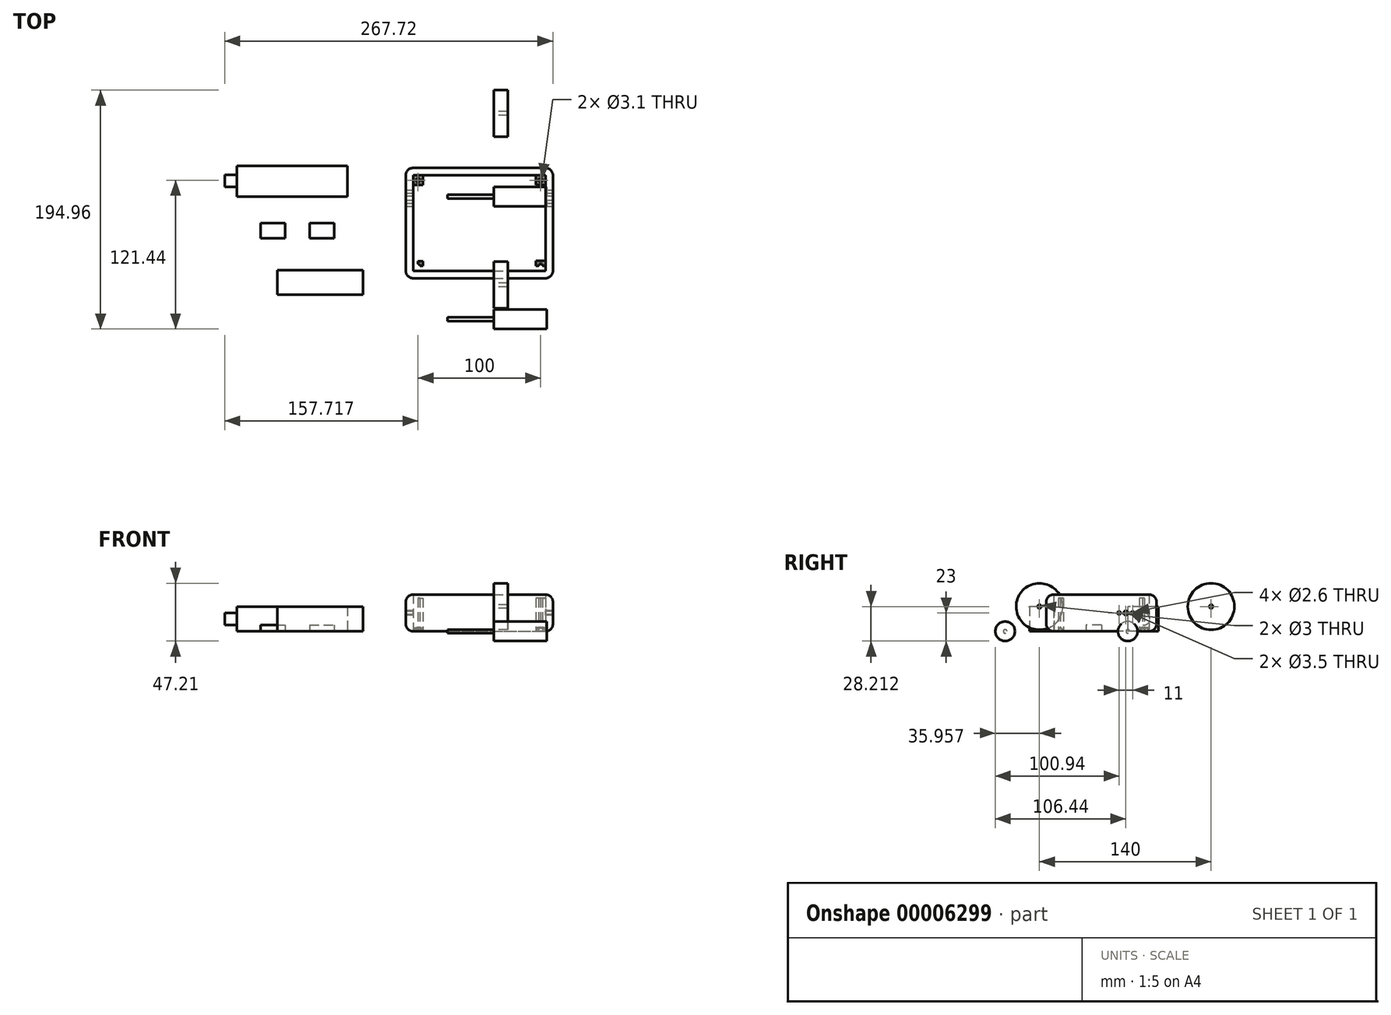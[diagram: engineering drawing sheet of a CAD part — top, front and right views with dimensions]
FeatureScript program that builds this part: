
annotation { "Feature Type Name" : "Feature", "Feature Type Description" : "" }
export const myFeature = defineFeature(function(context is Context, id is Id, definition is map)
    precondition{}
    {
        {
            var Q0;
            Q0=qCreatedBy(makeId("Top.planeOp"),FACE);
            var sketch = newSketch(context, id + "F0", { "sketchPlane" : qUnion([Q0])});
            skLineSegment(sketch, "E0.bottom", {"start": v(-71.87, 44.94) * mm, "end": v(48.13, 44.94) * mm});
            skLineSegment(sketch, "E0.top", {"start": v(-71.87, -45.06) * mm, "end": v(48.13, -45.06) * mm});
            skLineSegment(sketch, "E0.left", {"start": v(-71.87, 44.94) * mm, "end": v(-71.87, -45.06) * mm});
            skLineSegment(sketch, "E0.right", {"start": v(48.13, 44.94) * mm, "end": v(48.13, -45.06) * mm});
            skLineSegment(sketch, "E1.0", {"start": v(-65.87, 38.94) * mm, "end": v(42.13, 38.94) * mm});
            skLineSegment(sketch, "E1.1", {"start": v(-65.87, 38.94) * mm, "end": v(-65.87, -39.06) * mm});
            skLineSegment(sketch, "E1.2", {"start": v(-65.87, -39.06) * mm, "end": v(42.13, -39.06) * mm});
            skLineSegment(sketch, "E1.3", {"start": v(42.13, 38.94) * mm, "end": v(42.13, -39.06) * mm});
            skLineSegment(sketch, "E2.bottom", {"start": v(42.13, 38.94) * mm, "end": v(34.13, 38.94) * mm});
            skLineSegment(sketch, "E2.top", {"start": v(42.13, 30.94) * mm, "end": v(34.13, 30.94) * mm});
            skLineSegment(sketch, "E2.left", {"start": v(42.13, 38.94) * mm, "end": v(42.13, 30.94) * mm});
            skLineSegment(sketch, "E2.right", {"start": v(34.13, 38.94) * mm, "end": v(34.13, 30.94) * mm});
            skLineSegment(sketch, "E3.bottom", {"start": v(42.13, -39.06) * mm, "end": v(34.4, -39.06) * mm});
            skLineSegment(sketch, "E3.top", {"start": v(42.13, -31) * mm, "end": v(34.13, -31) * mm});
            skLineSegment(sketch, "E3.left", {"start": v(42.13, -39.06) * mm, "end": v(42.13, -31) * mm});
            skLineSegment(sketch, "E4.bottom", {"start": v(-65.87, 38.94) * mm, "end": v(-57.87, 38.94) * mm});
            skLineSegment(sketch, "E4.top", {"start": v(-65.87, 30.94) * mm, "end": v(-57.87, 30.94) * mm});
            skLineSegment(sketch, "E4.left", {"start": v(-65.87, 38.94) * mm, "end": v(-65.87, 30.94) * mm});
            skLineSegment(sketch, "E4.right", {"start": v(-57.87, 38.94) * mm, "end": v(-57.87, 30.94) * mm});
            skLineSegment(sketch, "E5.bottom", {"start": v(-65.87, -39.06) * mm, "end": v(-57.87, -39.06) * mm});
            skLineSegment(sketch, "E5.top", {"start": v(-65.87, -31.06) * mm, "end": v(-57.87, -31.06) * mm});
            skLineSegment(sketch, "E5.left", {"start": v(-65.87, -39.06) * mm, "end": v(-65.87, -31.06) * mm});
            skLineSegment(sketch, "E5.right", {"start": v(-57.87, -39.06) * mm, "end": v(-57.87, -31.06) * mm});
            skCircle(sketch, "E6", {"center": v(38.13, -35) * mm, "radius": 1.55 * mm});
            skLineSegment(sketch, "E7", {"start": v(38.13, -33.45) * mm, "end": v(38.13, -31) * mm});
            skCircle(sketch, "E8", {"center": v(38.13, 34.94) * mm, "radius": 1.55 * mm});
            skCircle(sketch, "E9", {"center": v(-61.87, 34.94) * mm, "radius": 1.55 * mm});
            skCircle(sketch, "E10", {"center": v(-61.87, -35.06) * mm, "radius": 1.55 * mm});
            skLineSegment(sketch, "E11", {"start": v(36.58, 34.94) * mm, "end": v(34.13, 34.94) * mm});
            skLineSegment(sketch, "E12", {"start": v(38.13, 33.4) * mm, "end": v(38.13, 30.94) * mm});
            skLineSegment(sketch, "E13", {"start": v(-60.32, 34.94) * mm, "end": v(-57.87, 34.94) * mm});
            skLineSegment(sketch, "E14", {"start": v(-61.87, 33.4) * mm, "end": v(-61.87, 30.94) * mm});
            skLineSegment(sketch, "E15", {"start": v(-61.87, -33.5) * mm, "end": v(-61.87, -31.06) * mm});
            skLineSegment(sketch, "E16", {"start": v(-60.32, -35.06) * mm, "end": v(-57.87, -35.06) * mm});
            skLineSegment(sketch, "E17", {"start": v(34.13, -31) * mm, "end": v(34.13, -39.06) * mm});
            skLineSegment(sketch, "E18", {"start": v(36.58, -35) * mm, "end": v(34.13, -35) * mm});
            skLineSegment(sketch, "E19", {"start": v(39.68, -35) * mm, "end": v(42.13, -35) * mm});
            skSolve(sketch);
        }
        {
            var Q0;
            Q0=makeQuery(id+"F0.imprint","IMPRINT",FACE,{"disambiguationData":[TD([[makeQuery(id+"F0.imprint","IMPRINT",EDGE,{"derivedFrom":sQuery(id+"F0.wireOp",EDGE,"E0.bottom")}),-1.0]])]});
            var Q1;
            {var subQ1=sQuery(id+"F0.wireOp",EDGE,"2364edff-3680-4c65-9d3e-53515021508b");Q1=makeQuery(id+"F0.imprint","IMPRINT",FACE,{"disambiguationData":[TD([[makeQuery(id+"F0.imprint","IMPRINT",EDGE,{"derivedFrom":subQ1}),-1.0]])]});}
            extrude(context, id + "F1", {"entities" : qUnion([Q0, Q1]), "depth" : 30 * mm});
        }
        {
            var Q0;
            {var subQ4=sQuery(id+"F0.wireOp",EDGE,"E4.bottom");Q0=makeQuery(id+"F0.imprint","IMPRINT",FACE,{"disambiguationData":[TD([[makeQuery(id+"F0.imprint","IMPRINT",EDGE,{"derivedFrom":subQ4}),-1.0]])]});}
            var Q1;
            {var subQ1=sQuery(id+"F0.wireOp",EDGE,"E13");Q1=makeQuery(id+"F0.imprint","IMPRINT",FACE,{"disambiguationData":[TD([[makeQuery(id+"F0.imprint","IMPRINT",EDGE,{"derivedFrom":subQ1}),-1.0]])]});}
            var Q2;
            {var subQ4=sQuery(id+"F0.wireOp",EDGE,"E2.bottom");Q2=makeQuery(id+"F0.imprint","IMPRINT",FACE,{"disambiguationData":[TD([[makeQuery(id+"F0.imprint","IMPRINT",EDGE,{"derivedFrom":subQ4}),1.0]])]});}
            var Q3;
            {var subQ1=sQuery(id+"F0.wireOp",EDGE,"E11");Q3=makeQuery(id+"F0.imprint","IMPRINT",FACE,{"disambiguationData":[TD([[makeQuery(id+"F0.imprint","IMPRINT",EDGE,{"derivedFrom":subQ1}),1.0]])]});}
            var Q4;
            {var subQ1=sQuery(id+"F0.wireOp",EDGE,"E7");Q4=makeQuery(id+"F0.imprint","IMPRINT",FACE,{"disambiguationData":[TD([[makeQuery(id+"F0.imprint","IMPRINT",EDGE,{"derivedFrom":subQ1}),-1.0]])]});}
            var Q5;
            {var subQ4=sQuery(id+"F0.wireOp",EDGE,"E7");Q5=makeQuery(id+"F0.imprint","IMPRINT",FACE,{"disambiguationData":[TD([[makeQuery(id+"F0.imprint","IMPRINT",EDGE,{"derivedFrom":subQ4}),1.0]])]});}
            var Q6;
            {var subQ7=sQuery(id+"F0.wireOp",EDGE,"E3.bottom");Q6=makeQuery(id+"F0.imprint","IMPRINT",FACE,{"disambiguationData":[TD([[makeQuery(id+"F0.imprint","IMPRINT",EDGE,{"derivedFrom":subQ7}),-1.0]])]});}
            var Q7;
            {var subQ1=sQuery(id+"F0.wireOp",EDGE,"E15");Q7=makeQuery(id+"F0.imprint","IMPRINT",FACE,{"disambiguationData":[TD([[makeQuery(id+"F0.imprint","IMPRINT",EDGE,{"derivedFrom":subQ1}),-1.0]])]});}
            var Q8;
            {var subQ4=sQuery(id+"F0.wireOp",EDGE,"E5.bottom");Q8=makeQuery(id+"F0.imprint","IMPRINT",FACE,{"disambiguationData":[TD([[makeQuery(id+"F0.imprint","IMPRINT",EDGE,{"derivedFrom":subQ4}),1.0]])]});}
            extrude(context, id + "F2", {"entities" : qUnion([Q0, Q1, Q2, Q3, Q4, Q5, Q6, Q7, Q8]), "operationType" : NewBodyOperationType.ADD, "depth" : 27 * mm});
        }
        {
            var Q0;
            {var subQ14=sQuery(id+"F0.wireOp",EDGE,"E1.0");Q0=makeQuery(id+"F0.imprint","IMPRINT",FACE,{"disambiguationData":[TD([[makeQuery(id+"F0.imprint","IMPRINT",EDGE,{"derivedFrom":subQ14}),-1.0]])]});}
            extrude(context, id + "F3", {"entities" : qUnion([Q0]), "operationType" : NewBodyOperationType.ADD, "depth" : 3 * mm});
        }
        {
            var Q0;
            Q0=makeQuery(id+"F1.opExtrude","SWEPT_EDGE",EDGE,{"disambiguationData":[OSD([sQuery(id+"F0.wireOp",EDGE,"E0.top"),sQuery(id+"F0.wireOp",EDGE,"E0.left")])]});
            var Q1;
            Q1=makeQuery(id+"F1.opExtrude","SWEPT_EDGE",EDGE,{"disambiguationData":[OSD([sQuery(id+"F0.wireOp",EDGE,"E0.top"),sQuery(id+"F0.wireOp",EDGE,"E0.right")])]});
            var Q2;
            Q2=makeQuery(id+"F1.opExtrude","SWEPT_EDGE",EDGE,{"disambiguationData":[OSD([sQuery(id+"F0.wireOp",EDGE,"E0.bottom"),sQuery(id+"F0.wireOp",EDGE,"E0.right")])]});
            var Q3;
            Q3=makeQuery(id+"F1.opExtrude","SWEPT_EDGE",EDGE,{"disambiguationData":[OSD([sQuery(id+"F0.wireOp",EDGE,"E0.bottom"),sQuery(id+"F0.wireOp",EDGE,"E0.left")])]});
            var Q4;
            Q4=makeQuery(id+"F1.opExtrude","CAP_EDGE",EDGE,{"disambiguationData":[OSD([sQuery(id+"F0.wireOp",EDGE,"E0.left")])],"isStart":false});
            var Q5;
            Q5=makeQuery(id+"F1.opExtrude","CAP_EDGE",EDGE,{"disambiguationData":[OSD([sQuery(id+"F0.wireOp",EDGE,"E0.right")])],"isStart":false});
            var Q6;
            Q6=makeQuery(id+"F1.opExtrude","CAP_EDGE",EDGE,{"disambiguationData":[OSD([sQuery(id+"F0.wireOp",EDGE,"E0.right")])],"isStart":true});
            var Q7;
            Q7=makeQuery(id+"F1.opExtrude","CAP_EDGE",EDGE,{"disambiguationData":[OSD([sQuery(id+"F0.wireOp",EDGE,"E0.left")])],"isStart":true});
            var Q8;
            Q8=makeQuery(id+"F1.opExtrude","CAP_EDGE",EDGE,{"disambiguationData":[OSD([sQuery(id+"F0.wireOp",EDGE,"E0.top")])],"isStart":false});
            var Q9;
            Q9=makeQuery(id+"F1.opExtrude","CAP_EDGE",EDGE,{"disambiguationData":[OSD([sQuery(id+"F0.wireOp",EDGE,"E0.bottom")])],"isStart":false});
            var Q10;
            Q10=makeQuery(id+"F1.opExtrude","CAP_EDGE",EDGE,{"disambiguationData":[OSD([sQuery(id+"F0.wireOp",EDGE,"E0.bottom")])],"isStart":true});
            var Q11;
            Q11=makeQuery(id+"F1.opExtrude","CAP_EDGE",EDGE,{"disambiguationData":[OSD([sQuery(id+"F0.wireOp",EDGE,"E0.top")])],"isStart":true});
            fillet(context, id + "F4", {"entities" : qUnion([Q0, Q1, Q2, Q3, Q4, Q5, Q6, Q7, Q8, Q9, Q10, Q11]), "radius" : 6 * mm, "tangentPropagation" : true, "allowEdgeOverflow" : false});
        }
        {
            var Q0;
            Q0=makeQuery(id+"F1.opExtrude","SWEPT_FACE",FACE,{"disambiguationData":[OSD([sQuery(id+"F0.wireOp",EDGE,"E0.left")])]});
            var sketch = newSketch(context, id + "F5", { "sketchPlane" : qUnion([Q0])});
            skCircle(sketch, "E20", {"center": v(-25.44, 15) * mm, "radius": 1.3 * mm});
            skCircle(sketch, "E21", {"center": v(-14.44, 15) * mm, "radius": 1.3 * mm});
            skCircle(sketch, "E22", {"center": v(-19.94, 15) * mm, "radius": 1.75 * mm});
            skLineSegment(sketch, "E23", {"start": v(-25.44, 15) * mm, "end": v(-19.94, 15) * mm, "construction": true});
            skLineSegment(sketch, "E24", {"start": v(-14.44, 15) * mm, "end": v(-19.94, 15) * mm, "construction": true});
            skLineSegment(sketch, "E25", {"start": v(-19.94, 15) * mm, "end": v(-19.94, 24) * mm, "construction": true});
            skLineSegment(sketch, "E26", {"start": v(-19.94, 24) * mm, "end": v(-19.94, 15) * mm, "construction": true});
            skLineSegment(sketch, "E27", {"start": v(-19.94, 15) * mm, "end": v(-19.94, 6) * mm, "construction": true});
            skSolve(sketch);
        }
        {
            var Q0;
            Q0=makeQuery(id+"F5.imprint","IMPRINT",FACE,{"disambiguationData":[TD([[makeQuery(id+"F5.imprint","IMPRINT",EDGE,{"derivedFrom":sQuery(id+"F5.wireOp",EDGE,"E22")}),1.0]])]});
            var Q1;
            Q1=makeQuery(id+"F5.imprint","IMPRINT",FACE,{"disambiguationData":[TD([[makeQuery(id+"F5.imprint","IMPRINT",EDGE,{"derivedFrom":sQuery(id+"F5.wireOp",EDGE,"E21")}),1.0]])]});
            var Q2;
            Q2=makeQuery(id+"F5.imprint","IMPRINT",FACE,{"disambiguationData":[TD([[makeQuery(id+"F5.imprint","IMPRINT",EDGE,{"derivedFrom":sQuery(id+"F5.wireOp",EDGE,"E20")}),1.0]])]});
            var Q3;
            Q3=sQuery(id+"F5.wireOp",EDGE,"E21");
            extrude(context, id + "F6", {"entities" : qUnion([Q0, Q1, Q2]), "operationType" : NewBodyOperationType.REMOVE, "surfaceEntities" : qUnion([Q3]), "endBound" : BoundingType.THROUGH_ALL, "oppositeDirection" : true, "depth" : 25 * mm});
        }
        {
            var Q0;
            Q0=qCreatedBy(makeId("Right.planeOp"),FACE);
            var sketch = newSketch(context, id + "F7", { "sketchPlane" : qUnion([Q0])});
            skCircle(sketch, "E28", {"center": v(-78.5, 0) * mm, "radius": 8 * mm});
            skSolve(sketch);
        }
        {
            var Q0;
            Q0 = qSketchRegion(id + "F7", true);
            extrude(context, id + "F8", {"entities" : qUnion([Q0]), "depth" : 43 * mm});
        }
        {
            var Q0;
            Q0=makeQuery(id+"F8.opExtrude","SWEPT_BODY",BODY,{"disambiguationData":[OSD([sQuery(id+"F7.wireOp",EDGE,"E28")])]});
            transform(context, id + "F9", {"entities" : qUnion([Q0]), "transformType" : TransformType.TRANSLATION_3D, "dx" : 0 * mm, "dy" : 100 * mm, "dz" : 0 * mm, "makeCopy" : true});
        }
        {
            var Q0;
            Q0=makeQuery(id+"F8.opExtrude","CAP_FACE",FACE,{"disambiguationData":[OSD([sQuery(id+"F7.wireOp",EDGE,"E28")])],"isStart":true});
            var sketch = newSketch(context, id + "F10", { "sketchPlane" : qUnion([Q0])});
            skCircle(sketch, "E29", {"center": v(78.5, 0) * mm, "radius": 1.5 * mm});
            skSolve(sketch);
        }
        {
            var Q0;
            Q0 = qSketchRegion(id + "F10", true);
            extrude(context, id + "F11", {"entities" : qUnion([Q0]), "operationType" : NewBodyOperationType.ADD, "depth" : 38 * mm});
        }
        {
            var Q0;
            Q0=makeQuery(id+"F9.opPattern","COPY",FACE,{"derivedFrom":makeQuery(id+"F8.opExtrude","CAP_FACE",FACE,{"disambiguationData":[OSD([sQuery(id+"F7.wireOp",EDGE,"E28")])],"isStart":true}),"instanceName":"1"});
            var sketch = newSketch(context, id + "F12", { "sketchPlane" : qUnion([Q0])});
            skCircle(sketch, "E30", {"center": v(-21.5, 0) * mm, "radius": 1.5 * mm});
            skSolve(sketch);
        }
        {
            var Q0;
            Q0 = qSketchRegion(id + "F12", true);
            extrude(context, id + "F13", {"entities" : qUnion([Q0]), "operationType" : NewBodyOperationType.ADD, "depth" : 38 * mm});
        }
        {
            var Q0;
            Q0=qCreatedBy(makeId("Right.planeOp"),FACE);
            var sketch = newSketch(context, id + "F14", { "sketchPlane" : qUnion([Q0])});
            skCircle(sketch, "E31", {"center": v(-50.54, 20.21) * mm, "radius": 19 * mm});
            skCircle(sketch, "E32", {"center": v(-50.54, 20.21) * mm, "radius": 1.5 * mm});
            skSolve(sketch);
        }
        {
            var Q0;
            Q0=makeQuery(id+"F14.imprint","IMPRINT",FACE,{"disambiguationData":[TD([[makeQuery(id+"F14.imprint","IMPRINT",EDGE,{"derivedFrom":sQuery(id+"F14.wireOp",EDGE,"E31")}),1.0]])]});
            var Q1;
            Q1 = qBodyType(qCreatedBy(id + "F14" ,EDGE), BodyType.WIRE);
            extrude(context, id + "F15", {"entities" : qUnion([Q0]), "surfaceEntities" : qUnion([Q1]), "depth" : 11.3 * mm});
        }
        {
            var Q0;
            Q0=makeQuery(id+"F15.opExtrude","SWEPT_BODY",BODY,{"disambiguationData":[OSD([sQuery(id+"F14.wireOp",EDGE,"E31"),sQuery(id+"F14.wireOp",EDGE,"E32")])]});
            transform(context, id + "F16", {"entities" : qUnion([Q0]), "transformType" : TransformType.TRANSLATION_3D, "dx" : 0 * mm, "dy" : 140 * mm, "dz" : 0 * mm, "makeCopy" : true});
        }
        {
            var Q0;
            Q0=qCreatedBy(makeId("Top.planeOp"),FACE);
            var sketch = newSketch(context, id + "F17", { "sketchPlane" : qUnion([Q0])});
            skLineSegment(sketch, "E33.bottom", {"start": v(-209.59, 46.54) * mm, "end": v(-119.59, 46.54) * mm});
            skLineSegment(sketch, "E33.top", {"start": v(-209.59, 21.54) * mm, "end": v(-119.59, 21.54) * mm});
            skLineSegment(sketch, "E33.left", {"start": v(-209.59, 46.54) * mm, "end": v(-209.59, 21.54) * mm});
            skLineSegment(sketch, "E33.right", {"start": v(-119.59, 46.54) * mm, "end": v(-119.59, 21.54) * mm});
            skSolve(sketch);
        }
        {
            var Q0;
            Q0 = qSketchRegion(id + "F17", true);
            extrude(context, id + "F18", {"entities" : qUnion([Q0]), "operationType" : NewBodyOperationType.ADD, "depth" : 20 * mm});
        }
        {
            var Q0;
            Q0=qCreatedBy(makeId("Top.planeOp"),FACE);
            var sketch = newSketch(context, id + "F19", { "sketchPlane" : qUnion([Q0])});
            skLineSegment(sketch, "E34.bottom", {"start": v(-176.7, -38.48) * mm, "end": v(-106.7, -38.48) * mm});
            skLineSegment(sketch, "E34.top", {"start": v(-176.7, -58.48) * mm, "end": v(-106.7, -58.48) * mm});
            skLineSegment(sketch, "E34.left", {"start": v(-176.7, -38.48) * mm, "end": v(-176.7, -58.48) * mm});
            skLineSegment(sketch, "E34.right", {"start": v(-106.7, -38.48) * mm, "end": v(-106.7, -58.48) * mm});
            skSolve(sketch);
        }
        {
            var Q0;
            Q0 = qSketchRegion(id + "F19", true);
            extrude(context, id + "F20", {"entities" : qUnion([Q0]), "depth" : 20 * mm});
        }
        {
            var Q0;
            Q0=makeQuery(id+"F18.opExtrude","SWEPT_FACE",FACE,{"disambiguationData":[OSD([sQuery(id+"F17.wireOp",EDGE,"E33.left")])]});
            var sketch = newSketch(context, id + "F21", { "sketchPlane" : qUnion([Q0])});
            skCircle(sketch, "E35", {"center": v(-34.44, 10.02) * mm, "radius": 5 * mm});
            skSolve(sketch);
        }
        {
            var Q0;
            Q0 = qSketchRegion(id + "F21", true);
            extrude(context, id + "F22", {"entities" : qUnion([Q0]), "operationType" : NewBodyOperationType.ADD, "depth" : 10 * mm});
        }
        {
            var Q0;
            Q0=qCreatedBy(makeId("Top.planeOp"),FACE);
            var sketch = newSketch(context, id + "F23", { "sketchPlane" : qUnion([Q0])});
            skLineSegment(sketch, "E36.bottom", {"start": v(-190.18, 0) * mm, "end": v(-170.18, 0) * mm});
            skLineSegment(sketch, "E36.top", {"start": v(-190.18, -12.5) * mm, "end": v(-170.18, -12.5) * mm});
            skLineSegment(sketch, "E36.left", {"start": v(-190.18, 0) * mm, "end": v(-190.18, -12.5) * mm});
            skLineSegment(sketch, "E36.right", {"start": v(-170.18, 0) * mm, "end": v(-170.18, -12.5) * mm});
            skSolve(sketch);
        }
        {
            var Q0;
            Q0 = qSketchRegion(id + "F23", true);
            extrude(context, id + "F24", {"entities" : qUnion([Q0]), "depth" : 5 * mm});
        }
        {
            var Q0;
            Q0=makeQuery(id+"F24.opExtrude","SWEPT_BODY",BODY,{"disambiguationData":[OSD([sQuery(id+"F23.wireOp",EDGE,"E36.bottom"),sQuery(id+"F23.wireOp",EDGE,"E36.top"),sQuery(id+"F23.wireOp",EDGE,"E36.left"),sQuery(id+"F23.wireOp",EDGE,"E36.right")])]});
            transform(context, id + "F25", {"entities" : qUnion([Q0]), "transformType" : TransformType.TRANSLATION_3D, "dx" : 40 * mm, "dy" : 0 * mm, "dz" : 0 * mm, "makeCopy" : true});
        }
        {
            var Q0;
            {var subQ14=sQuery(id+"F0.wireOp",EDGE,"E1.0");Q0=makeQuery(id+"F0.imprint","IMPRINT",FACE,{"disambiguationData":[TD([[makeQuery(id+"F0.imprint","IMPRINT",EDGE,{"derivedFrom":subQ14}),-1.0]])]});}
            var sketch = newSketch(context, id + "F26", { "sketchPlane" : qUnion([Q0])});
            skCircle(sketch, "E37.cCircle", {"center": v(-61.87, -35.06) * mm, "radius": 2.75 * mm, "construction": true});
            skLineSegment(sketch, "E37.0", {"start": v(-60.28, -32.3) * mm, "end": v(-58.7, -35.06) * mm});
            skLineSegment(sketch, "E37.1", {"start": v(-58.7, -35.06) * mm, "end": v(-60.28, -37.8) * mm});
            skLineSegment(sketch, "E37.2", {"start": v(-60.28, -37.8) * mm, "end": v(-63.46, -37.8) * mm});
            skLineSegment(sketch, "E37.3", {"start": v(-63.46, -37.8) * mm, "end": v(-65.05, -35.06) * mm});
            skLineSegment(sketch, "E37.4", {"start": v(-65.05, -35.06) * mm, "end": v(-63.46, -32.3) * mm});
            skLineSegment(sketch, "E37.5", {"start": v(-63.46, -32.3) * mm, "end": v(-60.28, -32.3) * mm});
            skPoint(sketch, "E37.0.midPoint", {"position": v(-59.5, -33.68) * mm});
            skCircle(sketch, "E38.cCircle", {"center": v(38.13, -35) * mm, "radius": 2.75 * mm, "construction": true});
            skLineSegment(sketch, "E38.0", {"start": v(36.54, -32.25) * mm, "end": v(39.72, -32.25) * mm});
            skLineSegment(sketch, "E38.1", {"start": v(39.72, -32.25) * mm, "end": v(41.3, -35) * mm});
            skLineSegment(sketch, "E38.2", {"start": v(41.3, -35) * mm, "end": v(39.72, -37.75) * mm});
            skLineSegment(sketch, "E38.3", {"start": v(39.72, -37.75) * mm, "end": v(36.54, -37.75) * mm});
            skLineSegment(sketch, "E38.4", {"start": v(36.54, -37.75) * mm, "end": v(34.95, -35) * mm});
            skLineSegment(sketch, "E38.5", {"start": v(34.95, -35) * mm, "end": v(36.54, -32.25) * mm});
            skPoint(sketch, "E38.0.midPoint", {"position": v(38.13, -32.25) * mm});
            skCircle(sketch, "E39.cCircle", {"center": v(-61.87, 34.94) * mm, "radius": 2.75 * mm, "construction": true});
            skLineSegment(sketch, "E39.0", {"start": v(-60.28, 37.7) * mm, "end": v(-58.7, 34.94) * mm});
            skLineSegment(sketch, "E39.1", {"start": v(-58.7, 34.94) * mm, "end": v(-60.28, 32.2) * mm});
            skLineSegment(sketch, "E39.2", {"start": v(-60.28, 32.2) * mm, "end": v(-63.46, 32.2) * mm});
            skLineSegment(sketch, "E39.3", {"start": v(-63.46, 32.2) * mm, "end": v(-65.05, 34.94) * mm});
            skLineSegment(sketch, "E39.4", {"start": v(-65.05, 34.94) * mm, "end": v(-63.46, 37.7) * mm});
            skLineSegment(sketch, "E39.5", {"start": v(-63.46, 37.7) * mm, "end": v(-60.28, 37.7) * mm});
            skPoint(sketch, "E39.0.midPoint", {"position": v(-59.5, 36.32) * mm});
            skCircle(sketch, "E40.cCircle", {"center": v(38.13, 34.94) * mm, "radius": 2.75 * mm, "construction": true});
            skLineSegment(sketch, "E40.0", {"start": v(36.54, 37.7) * mm, "end": v(39.72, 37.7) * mm});
            skLineSegment(sketch, "E40.1", {"start": v(39.72, 37.7) * mm, "end": v(41.3, 34.94) * mm});
            skLineSegment(sketch, "E40.2", {"start": v(41.3, 34.94) * mm, "end": v(39.72, 32.2) * mm});
            skLineSegment(sketch, "E40.3", {"start": v(39.72, 32.2) * mm, "end": v(36.54, 32.2) * mm});
            skLineSegment(sketch, "E40.4", {"start": v(36.54, 32.2) * mm, "end": v(34.95, 34.94) * mm});
            skLineSegment(sketch, "E40.5", {"start": v(34.95, 34.94) * mm, "end": v(36.54, 37.7) * mm});
            skPoint(sketch, "E40.0.midPoint", {"position": v(38.13, 37.7) * mm});
            skSolve(sketch);
        }
        {
            var Q0;
            Q0 = qSketchRegion(id + "F26", true);
            extrude(context, id + "F27", {"entities" : qUnion([Q0]), "operationType" : NewBodyOperationType.REMOVE, "depth" : 2.4 * mm});
        }
    });
